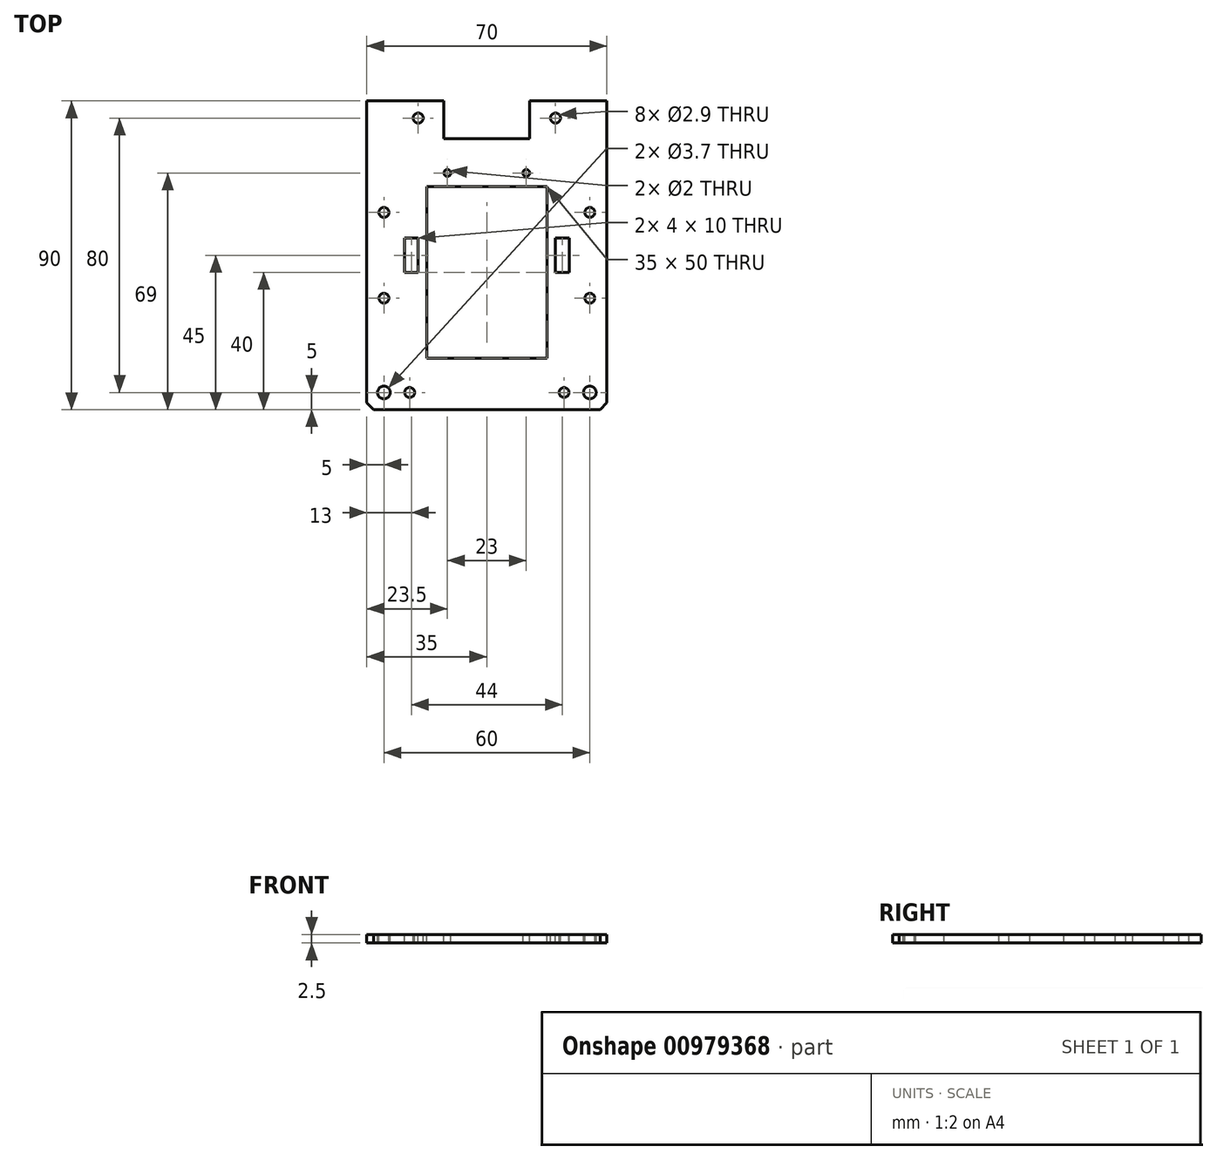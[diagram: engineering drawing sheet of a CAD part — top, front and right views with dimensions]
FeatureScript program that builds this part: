
annotation { "Feature Type Name" : "Feature", "Feature Type Description" : "" }
export const myFeature = defineFeature(function(context is Context, id is Id, definition is map)
    precondition{}
    {
        {
            var Q0;
            Q0=qCreatedBy(makeId("Top.planeOp"),FACE);
            var sketch = newSketch(context, id + "F0", { "sketchPlane" : qUnion([Q0])});
            skLineSegment(sketch, "E0.bottom", {"start": v(-35, 45) * mm, "end": v(35, 45) * mm});
            skLineSegment(sketch, "E0.top", {"start": v(-35, -45) * mm, "end": v(35, -45) * mm});
            skLineSegment(sketch, "E0.left", {"start": v(-35, 45) * mm, "end": v(-35, -45) * mm});
            skLineSegment(sketch, "E0.right", {"start": v(35, 45) * mm, "end": v(35, -45) * mm});
            skLineSegment(sketch, "E1.bottom", {"start": v(-11.5, 24) * mm, "end": v(11.5, 24) * mm, "construction": true});
            skLineSegment(sketch, "E1.top", {"start": v(-11.5, -34) * mm, "end": v(11.5, -34) * mm, "construction": true});
            skLineSegment(sketch, "E1.left", {"start": v(-11.5, 24) * mm, "end": v(-11.5, -34) * mm, "construction": true});
            skLineSegment(sketch, "E1.right", {"start": v(11.5, 24) * mm, "end": v(11.5, -34) * mm, "construction": true});
            skCircle(sketch, "E2", {"center": v(-11.5, 24) * mm, "radius": 1 * mm});
            skCircle(sketch, "E3.MirrorC", {"center": v(-11.5, -34) * mm, "radius": 1 * mm});
            skCircle(sketch, "E4", {"center": v(11.5, 24) * mm, "radius": 1 * mm});
            skCircle(sketch, "E5.MirrorC", {"center": v(11.5, -34) * mm, "radius": 1 * mm});
            skLineSegment(sketch, "E6", {"start": v(-12.5, 45) * mm, "end": v(-12.5, 34) * mm});
            skLineSegment(sketch, "E7", {"start": v(-12.5, 34) * mm, "end": v(12.5, 34) * mm});
            skLineSegment(sketch, "E8", {"start": v(12.5, 34) * mm, "end": v(12.5, 45) * mm});
            skCircle(sketch, "E9", {"center": v(-20, 40) * mm, "radius": 1.45 * mm});
            skCircle(sketch, "E10.MirrorC", {"center": v(20, 40) * mm, "radius": 1.45 * mm});
            skLineSegment(sketch, "E11", {"start": v(-20, 40) * mm, "end": v(20, 40) * mm, "construction": true});
            skLineSegment(sketch, "E12.bottom", {"start": v(-30, 12.5) * mm, "end": v(30, 12.5) * mm, "construction": true});
            skLineSegment(sketch, "E12.top", {"start": v(-30, -12.5) * mm, "end": v(30, -12.5) * mm, "construction": true});
            skLineSegment(sketch, "E12.left", {"start": v(-30, 12.5) * mm, "end": v(-30, -12.5) * mm, "construction": true});
            skLineSegment(sketch, "E12.right", {"start": v(30, 12.5) * mm, "end": v(30, -12.5) * mm, "construction": true});
            skCircle(sketch, "E13", {"center": v(-30, 12.5) * mm, "radius": 1.45 * mm});
            skCircle(sketch, "E14", {"center": v(30, 12.5) * mm, "radius": 1.45 * mm});
            skCircle(sketch, "E15", {"center": v(-30, -12.5) * mm, "radius": 1.45 * mm});
            skCircle(sketch, "E16", {"center": v(30, -12.5) * mm, "radius": 1.45 * mm});
            skLineSegment(sketch, "E17", {"start": v(-22.5, -40) * mm, "end": v(22.5, -40) * mm, "construction": true});
            skCircle(sketch, "E18", {"center": v(-22.5, -40) * mm, "radius": 1.45 * mm});
            skCircle(sketch, "E19", {"center": v(22.5, -40) * mm, "radius": 1.45 * mm});
            skLineSegment(sketch, "E20.bottom", {"start": v(-24, 5) * mm, "end": v(-20, 5) * mm});
            skLineSegment(sketch, "E20.top", {"start": v(-24, -5) * mm, "end": v(-20, -5) * mm});
            skLineSegment(sketch, "E20.left", {"start": v(-24, 5) * mm, "end": v(-24, -5) * mm});
            skLineSegment(sketch, "E20.right", {"start": v(-20, 5) * mm, "end": v(-20, -5) * mm});
            skLineSegment(sketch, "E21.MirrorCS", {"start": v(20, 5) * mm, "end": v(20, -5) * mm});
            skLineSegment(sketch, "E22.MirrorCS", {"start": v(24, -5) * mm, "end": v(20, -5) * mm});
            skLineSegment(sketch, "E23.MirrorCS", {"start": v(24, 5) * mm, "end": v(20, 5) * mm});
            skLineSegment(sketch, "E24.MirrorCS", {"start": v(24, 5) * mm, "end": v(24, -5) * mm});
            skLineSegment(sketch, "E25.bottom", {"start": v(-17.5, 20) * mm, "end": v(17.5, 20) * mm});
            skLineSegment(sketch, "E25.top", {"start": v(-17.5, -30) * mm, "end": v(17.5, -30) * mm});
            skLineSegment(sketch, "E25.left", {"start": v(-17.5, 20) * mm, "end": v(-17.5, -30) * mm});
            skLineSegment(sketch, "E25.right", {"start": v(17.5, 20) * mm, "end": v(17.5, -30) * mm});
            skLineSegment(sketch, "E26", {"start": v(-17.5, -5) * mm, "end": v(17.5, -5) * mm, "construction": true});
            skPoint(sketch, "E27", {"position": v(-11.5, -5) * mm});
            skCircle(sketch, "E28", {"center": v(-30, -40) * mm, "radius": 1.85 * mm});
            skCircle(sketch, "E29.MirrorC", {"center": v(30, -40) * mm, "radius": 1.85 * mm});
            skSolve(sketch);
        }
        {
            var Q0;
            {var subQ0=sQuery(id+"F0.wireOp",EDGE,"FdppKnC7-chlW-L3gS-RKyD-pVx7Mm1IkckR.bottom");Q0=makeQuery(id+"F0.imprint","IMPRINT",FACE,{"disambiguationData":[TD([[makeQuery(id+"F0.imprint","IMPRINT",EDGE,{"derivedFrom":subQ0}),-1.0]])]});}
            var Q1;
            {var subQ0=sQuery(id+"F0.wireOp",EDGE,"OX8sbtim-JhYk-IE1q-8thM-soOQ3miKd63f.bottom");var subQ1=sQuery(id+"F0.wireOp",EDGE,"FdppKnC7-chlW-L3gS-RKyD-pVx7Mm1IkckR.left");var subQ2=makeQuery(id+"F0.imprint","INTERSECT",VERTEX,{"derivedFrom":[subQ1,subQ0]});Q1=makeQuery(id+"F0.imprint","IMPRINT",FACE,{"disambiguationData":[TD([[makeQuery(id+"F0.imprint","IMPRINT",EDGE,{"disambiguationData":[TD([[subQ2,-1.0]])],"derivedFrom":subQ1}),1.0]])]});}
            var Q2;
            {var subQ5=sQuery(id+"F0.wireOp",EDGE,"OX8sbtim-JhYk-IE1q-8thM-soOQ3miKd63f.left");Q2=makeQuery(id+"F0.imprint","IMPRINT",FACE,{"disambiguationData":[TD([[makeQuery(id+"F0.imprint","IMPRINT",EDGE,{"derivedFrom":subQ5}),1.0]])]});}
            var Q3;
            {var subQ5=sQuery(id+"F0.wireOp",EDGE,"OX8sbtim-JhYk-IE1q-8thM-soOQ3miKd63f.right");Q3=makeQuery(id+"F0.imprint","IMPRINT",FACE,{"disambiguationData":[TD([[makeQuery(id+"F0.imprint","IMPRINT",EDGE,{"derivedFrom":subQ5}),-1.0]])]});}
            var Q4;
            {var subQ0=sQuery(id+"F0.wireOp",EDGE,"FdppKnC7-chlW-L3gS-RKyD-pVx7Mm1IkckR.top");Q4=makeQuery(id+"F0.imprint","IMPRINT",FACE,{"disambiguationData":[TD([[makeQuery(id+"F0.imprint","IMPRINT",EDGE,{"derivedFrom":subQ0}),1.0]])]});}
            var Q5;
            Q5=makeQuery(id+"F0.imprint","IMPRINT",FACE,{"disambiguationData":[TD([[makeQuery(id+"F0.imprint","IMPRINT",EDGE,{"derivedFrom":sQuery(id+"F0.wireOp",EDGE,"E2")}),-1.0]])]});
            var Q6;
            Q6=makeQuery(id+"F0.imprint","IMPRINT",FACE,{"disambiguationData":[TD([[makeQuery(id+"F0.imprint","IMPRINT",EDGE,{"derivedFrom":sQuery(id+"F0.wireOp",EDGE,"E4")}),-1.0]])]});
            var Q7;
            Q7=makeQuery(id+"F0.imprint","IMPRINT",FACE,{"disambiguationData":[TD([[makeQuery(id+"F0.imprint","IMPRINT",EDGE,{"derivedFrom":sQuery(id+"F0.wireOp",EDGE,"Q1nGrmMh-5gD4-jKZR-ydbN-ikoJonWVVyY7")}),-1.0]])]});
            var Q8;
            Q8=makeQuery(id+"F0.imprint","IMPRINT",FACE,{"disambiguationData":[TD([[makeQuery(id+"F0.imprint","IMPRINT",EDGE,{"derivedFrom":sQuery(id+"F0.wireOp",EDGE,"9290bae9-4108-471e-960f-4acc042b23630.MirrorC")}),1.0]])]});
            var Q9;
            Q9=makeQuery(id+"F0.imprint","IMPRINT",FACE,{"disambiguationData":[TD([[makeQuery(id+"F0.imprint","IMPRINT",EDGE,{"derivedFrom":sQuery(id+"F0.wireOp",EDGE,"5b7e9a47-df9d-4a0a-bc5b-0726ed72bcd60.MirrorC")}),1.0]])]});
            var Q10;
            Q10=makeQuery(id+"F0.imprint","IMPRINT",FACE,{"disambiguationData":[TD([[makeQuery(id+"F0.imprint","IMPRINT",EDGE,{"derivedFrom":sQuery(id+"F0.wireOp",EDGE,"YeZDzGO2-CeeO-901W-CBWX-nhvC6mvGDPlY")}),-1.0]])]});
            var Q11;
            Q11=makeQuery(id+"F0.imprint","IMPRINT",FACE,{"disambiguationData":[TD([[makeQuery(id+"F0.imprint","IMPRINT",EDGE,{"derivedFrom":sQuery(id+"F0.wireOp",EDGE,"E3.MirrorC")}),1.0]])]});
            var Q12;
            Q12=makeQuery(id+"F0.imprint","IMPRINT",FACE,{"disambiguationData":[TD([[makeQuery(id+"F0.imprint","IMPRINT",EDGE,{"derivedFrom":sQuery(id+"F0.wireOp",EDGE,"E5.MirrorC")}),1.0]])]});
            var Q13;
            Q13=makeQuery(id+"F0.imprint","IMPRINT",FACE,{"disambiguationData":[TD([[makeQuery(id+"F0.imprint","IMPRINT",EDGE,{"derivedFrom":sQuery(id+"F0.wireOp",EDGE,"E0.top")}),1.0]])]});
            extrude(context, id + "F1", {"entities" : qUnion([Q0, Q1, Q2, Q3, Q4, Q5, Q6, Q7, Q8, Q9, Q10, Q11, Q12, Q13]), "oppositeDirection" : true, "depth" : 2.5 * mm, "offsetDistance" : 25 * mm});
        }
        {
            var Q0;
            Q0=makeQuery(id+"F1.opExtrude","SWEPT_EDGE",EDGE,{"disambiguationData":[OSD([sQuery(id+"F0.wireOp",EDGE,"E0.top"),sQuery(id+"F0.wireOp",EDGE,"E0.left")])]});
            var Q1;
            Q1=makeQuery(id+"F1.opExtrude","SWEPT_EDGE",EDGE,{"disambiguationData":[OSD([sQuery(id+"F0.wireOp",EDGE,"E0.top"),sQuery(id+"F0.wireOp",EDGE,"E0.right")])]});
            chamfer(context, id + "F2", {"entities" : qUnion([Q0, Q1]), "width" : 2 * mm, "tangentPropagation" : true});
        }
    });
